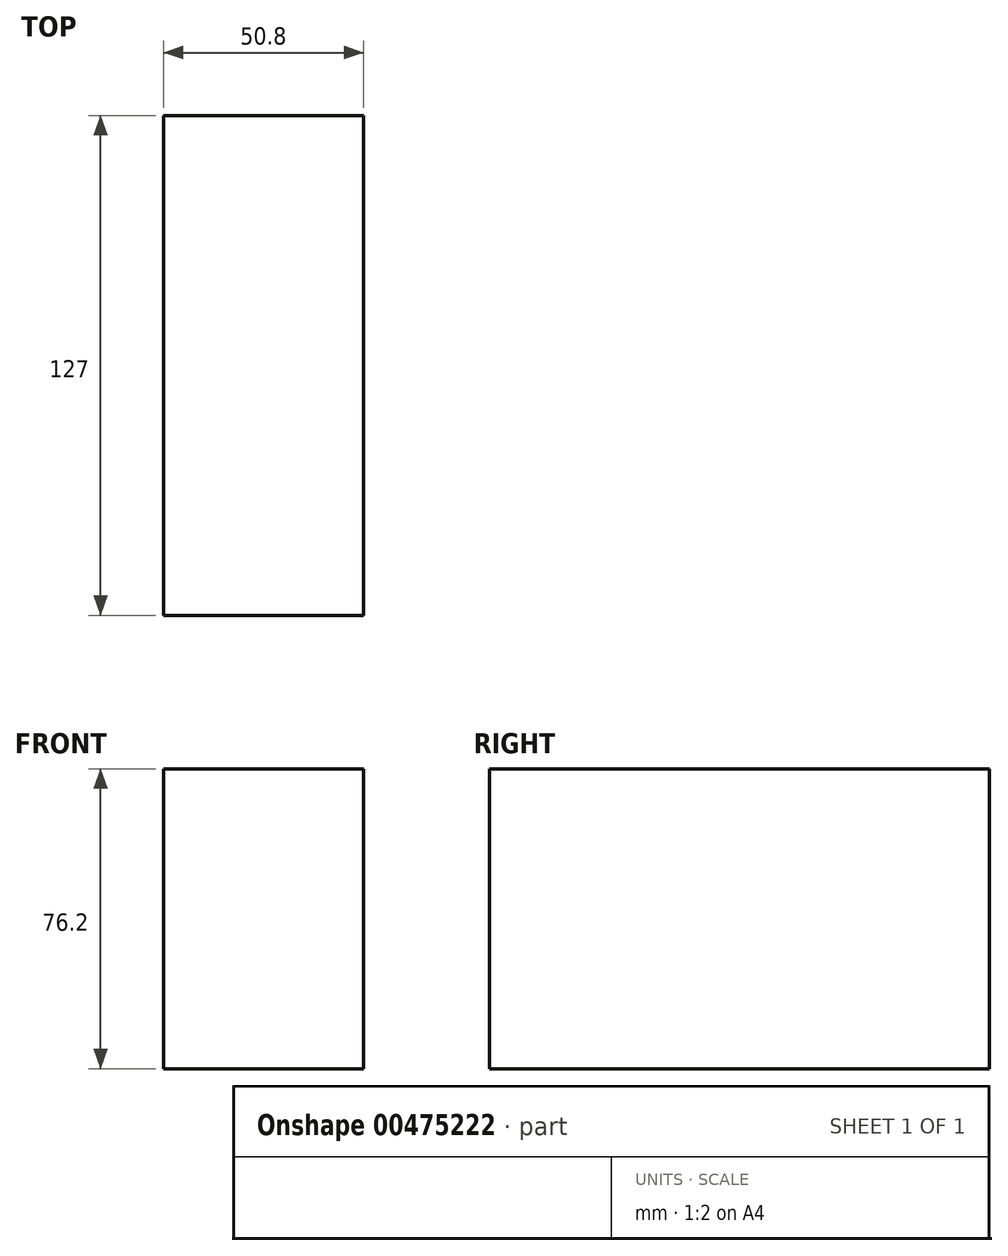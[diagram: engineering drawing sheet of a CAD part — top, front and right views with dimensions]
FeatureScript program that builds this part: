
annotation { "Feature Type Name" : "Feature", "Feature Type Description" : "" }
export const myFeature = defineFeature(function(context is Context, id is Id, definition is map)
    precondition{}
    {
        {
            var Q0;
            Q0=qCreatedBy(makeId("Front.planeOp"),FACE);
            var sketch = newSketch(context, id + "F0", { "sketchPlane" : qUnion([Q0])});
            skLineSegment(sketch, "E0.bottom", {"start": v(25.4, 38.1) * mm, "end": v(-25.4, 38.1) * mm});
            skLineSegment(sketch, "E0.top", {"start": v(25.4, -38.1) * mm, "end": v(-25.4, -38.1) * mm});
            skLineSegment(sketch, "E0.left", {"start": v(25.4, 38.1) * mm, "end": v(25.4, -38.1) * mm});
            skLineSegment(sketch, "E0.right", {"start": v(-25.4, 38.1) * mm, "end": v(-25.4, -38.1) * mm});
            skPoint(sketch, "E0.middle", {"position": v(0, 0) * mm});
            skSolve(sketch);
        }
        {
            var Q0;
            Q0 = qSketchRegion(id + "F0", true);
            extrude(context, id + "F1", {"entities" : qUnion([Q0]), "endBound" : BoundingType.SYMMETRIC, "depth" : 127 * mm});
        }
    });
